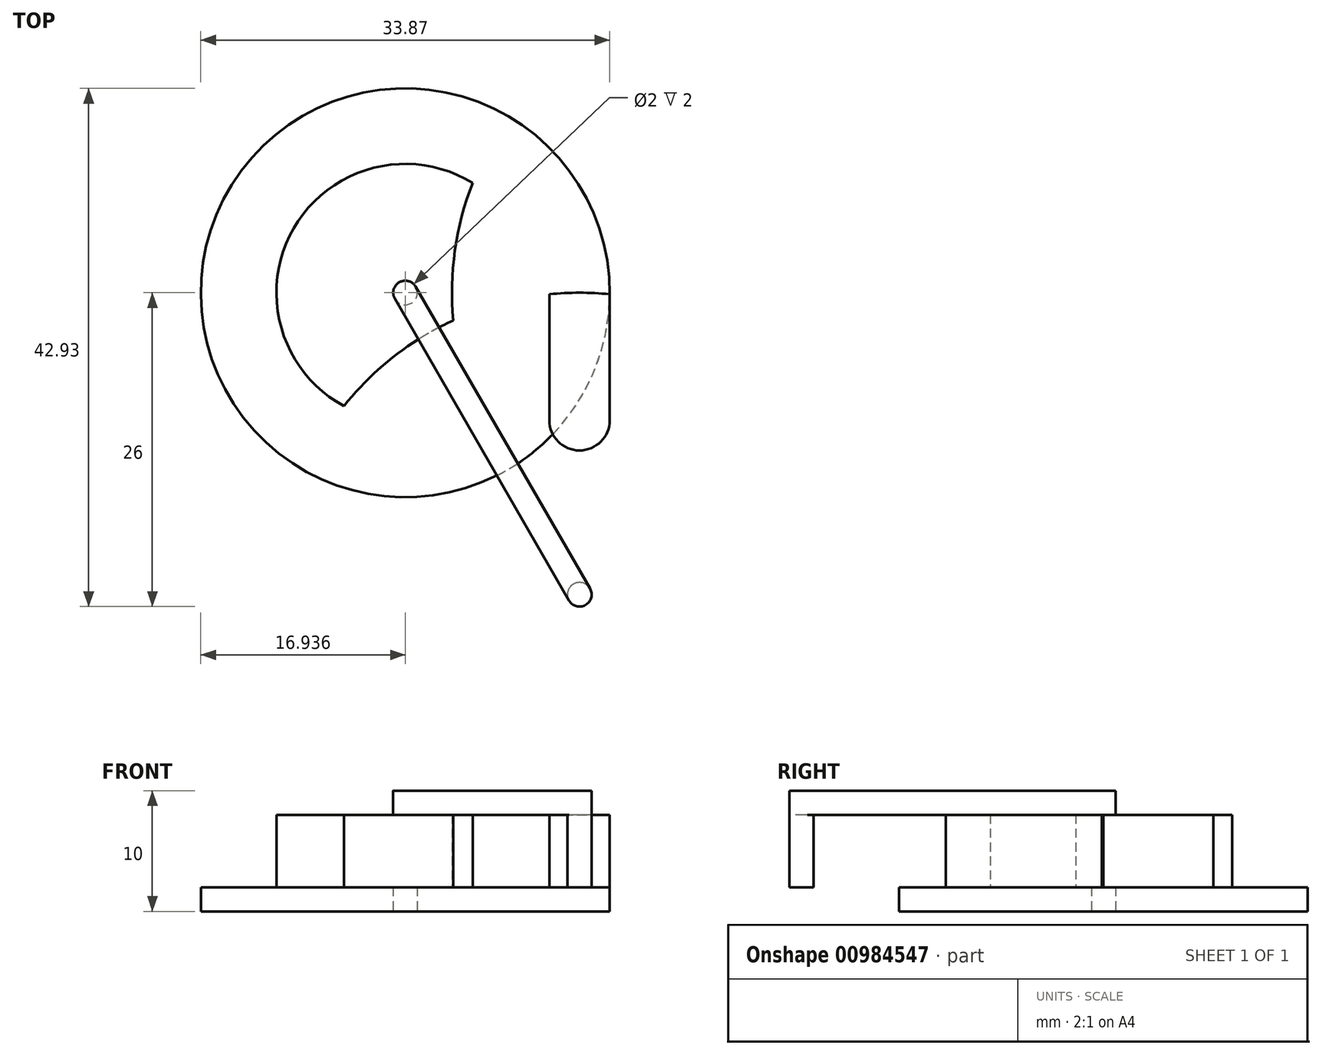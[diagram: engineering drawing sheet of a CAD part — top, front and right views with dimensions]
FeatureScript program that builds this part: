
annotation { "Feature Type Name" : "Feature", "Feature Type Description" : "" }
export const myFeature = defineFeature(function(context is Context, id is Id, definition is map)
    precondition{}
    {
        {
            var Q0;
            Q0=qCreatedBy(makeId("Top.planeOp"),FACE);
            var sketch = newSketch(context, id + "F0", { "sketchPlane" : qUnion([Q0])});
            skCircle(sketch, "E0", {"center": v(0, 0) * mm, "radius": 25 * mm});
            skCircle(sketch, "E1", {"center": v(0, 25) * mm, "radius": 2.5 * mm});
            skCircle(sketch, "E2", {"center": v(-14.43, 25) * mm, "radius": 10.67 * mm});
            skCircle(sketch, "E3", {"center": v(-14.43, 25) * mm, "radius": 14.43 * mm, "construction": true});
            skLineSegment(sketch, "E4", {"start": v(-14.43, 25) * mm, "end": v(-7.22, 12.5) * mm, "construction": true});
            skLineSegment(sketch, "E5", {"start": v(0, 25) * mm, "end": v(0, 14.43) * mm, "construction": true});
            skArc(sketch, "E6.0.startCap", {"start": v(-2.5, 25) * mm, "mid": v(0, 27.5) * mm, "end": v(2.5, 25) * mm});
            skArc(sketch, "E6.0.endCap", {"start": v(2.5, 14.43) * mm, "mid": v(0, 11.93) * mm, "end": v(-2.5, 14.43) * mm});
            skLineSegment(sketch, "E6.0.left", {"start": v(2.5, 25) * mm, "end": v(2.5, 14.43) * mm});
            skLineSegment(sketch, "E6.0.right", {"start": v(-2.5, 25) * mm, "end": v(-2.5, 14.43) * mm});
            skCircle(sketch, "E7", {"center": v(0, 0) * mm, "radius": 14.43 * mm, "construction": true});
            skCircle(sketch, "E8", {"center": v(0, 0) * mm, "radius": 1 * mm});
            skCircle(sketch, "E9", {"center": v(-14.43, 25) * mm, "radius": 1 * mm});
            skLineSegment(sketch, "E10.1.0", {"start": v(-20.4, 14.67) * mm, "end": v(-11.25, 9.38) * mm});
            skLineSegment(sketch, "E10.1.1", {"start": v(-22.9, 10.33) * mm, "end": v(-13.75, 5.05) * mm});
            skArc(sketch, "E10.1.2", {"start": v(-11.25, 9.38) * mm, "mid": v(-10.33, 5.97) * mm, "end": v(-13.75, 5.05) * mm});
            skCircle(sketch, "E10.1.3", {"center": v(-28.87, 0) * mm, "radius": 10.67 * mm});
            skCircle(sketch, "E10.1.4", {"center": v(-21.65, 12.5) * mm, "radius": 2.5 * mm});
            skLineSegment(sketch, "E10.2.0", {"start": v(-22.9, -10.33) * mm, "end": v(-13.75, -5.05) * mm});
            skLineSegment(sketch, "E10.2.1", {"start": v(-20.4, -14.67) * mm, "end": v(-11.25, -9.38) * mm});
            skArc(sketch, "E10.2.2", {"start": v(-13.75, -5.05) * mm, "mid": v(-10.33, -5.97) * mm, "end": v(-11.25, -9.38) * mm});
            skCircle(sketch, "E10.2.3", {"center": v(-14.43, -25) * mm, "radius": 10.67 * mm});
            skCircle(sketch, "E10.2.4", {"center": v(-21.65, -12.5) * mm, "radius": 2.5 * mm});
            skArc(sketch, "E11", {"start": v(-8.85, 34.1) * mm, "mid": v(-10.57, 25) * mm, "end": v(-8.85, 15.9) * mm});
            skLineSegment(sketch, "E12.3.3.0", {"start": v(2.5, -25) * mm, "end": v(2.5, -14.43) * mm});
            skArc(sketch, "E12.6.3.0", {"start": v(-2.5, -14.43) * mm, "mid": v(0, -11.93) * mm, "end": v(2.5, -14.43) * mm});
            skCircle(sketch, "E12.10.3.0", {"center": v(14.43, -25) * mm, "radius": 10.67 * mm});
            skLineSegment(sketch, "E12.11.3.0", {"start": v(-2.5, -25) * mm, "end": v(-2.5, -14.43) * mm});
            skCircle(sketch, "E12.12.3.0", {"center": v(0, -25) * mm, "radius": 2.5 * mm});
            skLineSegment(sketch, "E13.3.4.0", {"start": v(22.9, -10.33) * mm, "end": v(13.75, -5.05) * mm});
            skArc(sketch, "E13.6.4.0", {"start": v(11.25, -9.38) * mm, "mid": v(10.33, -5.97) * mm, "end": v(13.75, -5.05) * mm});
            skCircle(sketch, "E13.10.4.0", {"center": v(28.87, 0) * mm, "radius": 10.67 * mm});
            skLineSegment(sketch, "E13.11.4.0", {"start": v(20.4, -14.67) * mm, "end": v(11.25, -9.38) * mm});
            skCircle(sketch, "E13.12.4.0", {"center": v(21.65, -12.5) * mm, "radius": 2.5 * mm});
            skLineSegment(sketch, "E13.3.5.0", {"start": v(20.4, 14.67) * mm, "end": v(11.25, 9.38) * mm});
            skArc(sketch, "E13.6.5.0", {"start": v(13.75, 5.05) * mm, "mid": v(10.33, 5.97) * mm, "end": v(11.25, 9.38) * mm});
            skCircle(sketch, "E13.10.5.0", {"center": v(14.43, 25) * mm, "radius": 10.67 * mm});
            skLineSegment(sketch, "E13.11.5.0", {"start": v(22.9, 10.33) * mm, "end": v(13.75, 5.05) * mm});
            skCircle(sketch, "E13.12.5.0", {"center": v(21.65, 12.5) * mm, "radius": 2.5 * mm});
            skSolve(sketch);
        }
        {
            var Q0;
            {var subQ22=sQuery(id+"F0.wireOp",EDGE,"E6.0.endCap");Q0=makeQuery(id+"F0.imprint","IMPRINT",FACE,{"disambiguationData":[TD([[makeQuery(id+"F0.imprint","IMPRINT",EDGE,{"derivedFrom":subQ22}),1.0]])]});}
            var Q1;
            Q1=makeQuery(id+"F0.imprint","IMPRINT",FACE,{"disambiguationData":[TD([[makeQuery(id+"F0.imprint","IMPRINT",EDGE,{"derivedFrom":sQuery(id+"F0.wireOp",EDGE,"E9")}),1.0]])]});
            extrude(context, id + "F1", {"entities" : qUnion([Q0, Q1]), "endBound" : BoundingType.SYMMETRIC, "depth" : 6 * mm, "offsetDistance" : 25 * mm});
        }
        {
            var Q0;
            {var subQ0=sQuery(id+"F0.wireOp",EDGE,"E1");var subQ1=makeQuery(id+"F0.imprint","INTERSECT",VERTEX,{"derivedFrom":[subQ0,sQuery(id+"F0.wireOp",EDGE,"E6.0.left")]});Q0=makeQuery(id+"F0.imprint","IMPRINT",FACE,{"disambiguationData":[TD([[makeQuery(id+"F0.imprint","IMPRINT",EDGE,{"disambiguationData":[TD([[subQ1,-1.0]])],"derivedFrom":subQ0}),1.0]])]});}
            var Q1;
            Q1=makeQuery(id+"F0.imprint","IMPRINT",FACE,{"disambiguationData":[TD([[makeQuery(id+"F0.imprint","IMPRINT",EDGE,{"derivedFrom":sQuery(id+"F0.wireOp",EDGE,"E8")}),1.0]])]});
            var Q2;
            Q2=makeQuery(id+"F0.imprint","IMPRINT",FACE,{"disambiguationData":[TD([[makeQuery(id+"F0.imprint","IMPRINT",EDGE,{"derivedFrom":sQuery(id+"F0.wireOp",EDGE,"E9")}),-1.0]])]});
            var Q3;
            {var subQ0=sQuery(id+"F0.wireOp",EDGE,"E1");var subQ1=sQuery(id+"F0.wireOp",EDGE,"E0");var subQ2=makeQuery(id+"F0.imprint","INTERSECT",VERTEX,{"disambiguationData":[OD(0.0)],"derivedFrom":[subQ1,subQ0]});Q3=makeQuery(id+"F0.imprint","IMPRINT",FACE,{"disambiguationData":[TD([[makeQuery(id+"F0.imprint","IMPRINT",EDGE,{"disambiguationData":[TD([[subQ2,-1.0]])],"derivedFrom":subQ1}),1.0]])]});}
            extrude(context, id + "F2", {"entities" : qUnion([Q0, Q1, Q2, Q3]), "endBound" : BoundingType.SYMMETRIC, "depth" : 6 * mm, "offsetDistance" : 25 * mm});
        }
        {
            var Q0;
            Q0=makeQuery(id+"F2.opExtrude","CAP_FACE",FACE,{"disambiguationData":[OSD([sQuery(id+"F0.wireOp",EDGE,"E2"),sQuery(id+"F0.wireOp",EDGE,"E9")])],"isStart":true});
            var sketch = newSketch(context, id + "F3", { "sketchPlane" : qUnion([Q0])});
            skCircle(sketch, "E14", {"center": v(-14.43, -25) * mm, "radius": 16.93 * mm});
            skSolve(sketch);
        }
        {
            var Q0;
            Q0=makeQuery(id+"F3.imprint","IMPRINT",FACE,{"disambiguationData":[TD([[makeQuery(id+"F3.imprint","IMPRINT",EDGE,{"derivedFrom":sQuery(id+"F3.wireOp",EDGE,"E14")}),1.0]])]});
            var Q1;
            Q1=makeQuery(id+"F3.imprint","IMPRINT",FACE,{"disambiguationData":[TD([[makeQuery(id+"F3.imprint","IMPRINT",EDGE,{"derivedFrom":makeQuery(id+"F2.opExtrude","CAP_EDGE",EDGE,{"disambiguationData":[OSD([sQuery(id+"F0.wireOp",EDGE,"E2")])],"isStart":false})}),1.0]])]});
            var Q2;
            Q2=makeQuery(id+"F3.imprint","IMPRINT",FACE,{"disambiguationData":[TD([[makeQuery(id+"F3.imprint","IMPRINT",EDGE,{"derivedFrom":makeQuery(id+"F2.opExtrude","CAP_EDGE",EDGE,{"disambiguationData":[OSD([sQuery(id+"F0.wireOp",EDGE,"E2")])],"isStart":true})}),-1.0]])]});
            extrude(context, id + "F4", {"entities" : qUnion([Q0, Q1, Q2]), "operationType" : NewBodyOperationType.ADD, "depth" : 2 * mm, "offsetDistance" : 25 * mm});
        }
        {
            var Q0;
            Q0=makeQuery(id+"F1.opExtrude","CAP_FACE",FACE,{"disambiguationData":[OSD([sQuery(id+"F0.wireOp",EDGE,"E9")])],"isStart":false});
            var sketch = newSketch(context, id + "F5", { "sketchPlane" : qUnion([Q0])});
            skLineSegment(sketch, "E15", {"start": v(-14.43, 25) * mm, "end": v(0, 0) * mm, "construction": true});
            skArc(sketch, "E16.0.startCap", {"start": v(-15.3, 24.5) * mm, "mid": v(-14.93, 25.87) * mm, "end": v(-13.57, 25.5) * mm});
            skArc(sketch, "E16.0.endCap", {"start": v(0.87, 0.5) * mm, "mid": v(0.5, -0.87) * mm, "end": v(-0.87, -0.5) * mm});
            skLineSegment(sketch, "E16.0.left", {"start": v(-13.57, 25.5) * mm, "end": v(0.87, 0.5) * mm});
            skLineSegment(sketch, "E16.0.right", {"start": v(-15.3, 24.5) * mm, "end": v(-0.87, -0.5) * mm});
            skSolve(sketch);
        }
        {
            var Q0;
            Q0 = qSketchRegion(id + "F5", true);
            extrude(context, id + "F6", {"entities" : qUnion([Q0]), "operationType" : NewBodyOperationType.ADD, "depth" : 2 * mm, "offsetDistance" : 25 * mm});
        }
    });
